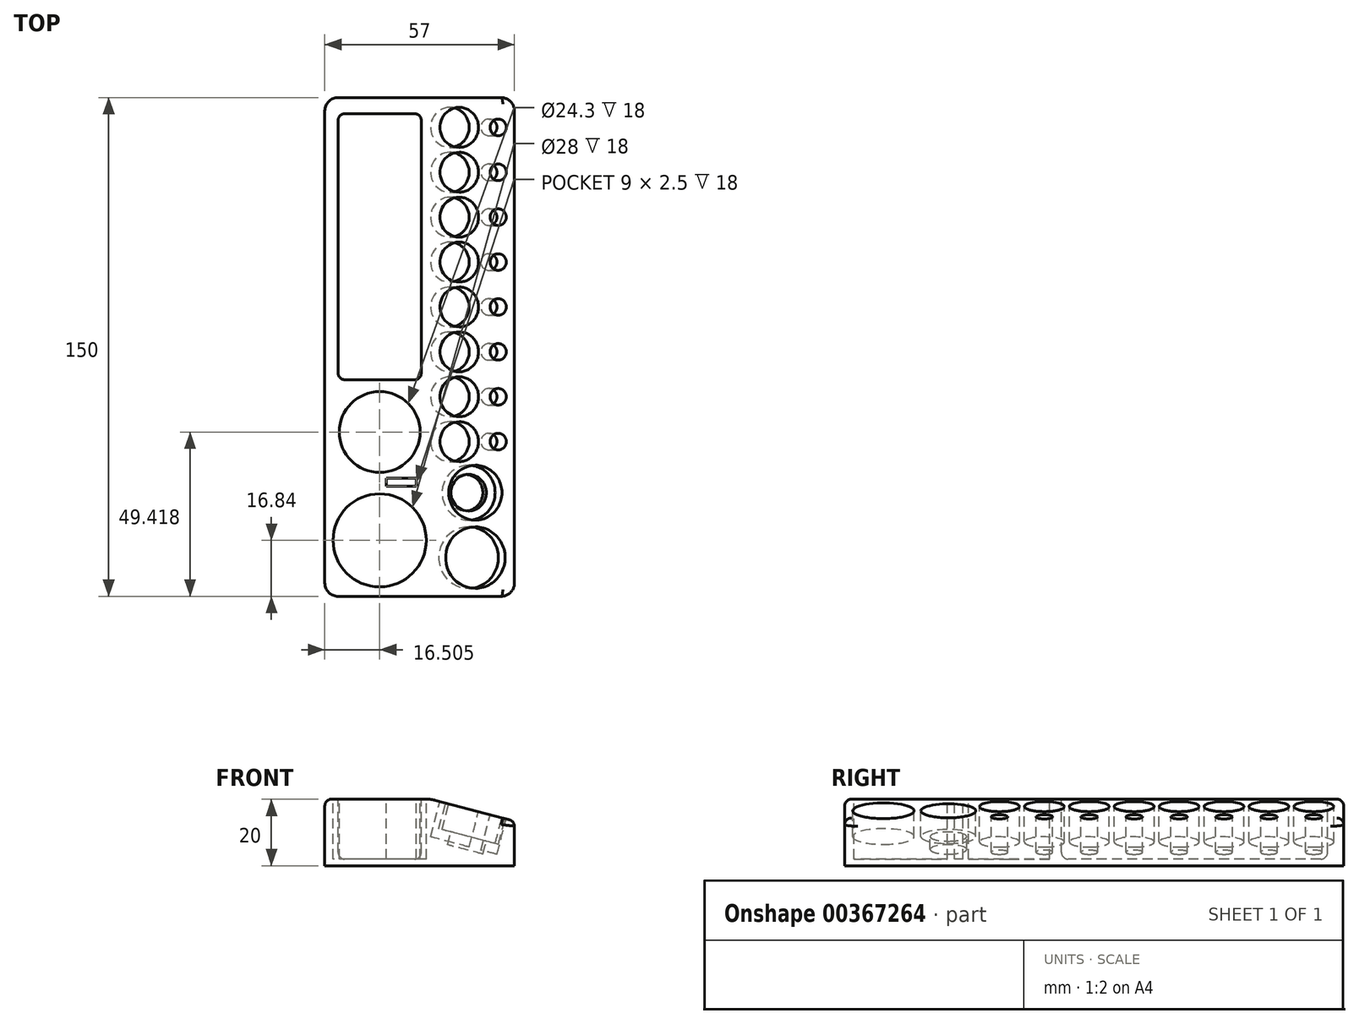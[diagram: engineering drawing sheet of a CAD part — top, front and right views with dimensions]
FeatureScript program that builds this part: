
annotation { "Feature Type Name" : "Feature", "Feature Type Description" : "" }
export const myFeature = defineFeature(function(context is Context, id is Id, definition is map)
    precondition{}
    {
        {
            var Q0;
            Q0=qCreatedBy(makeId("Front.planeOp"),FACE);
            var sketch = newSketch(context, id + "F0", { "sketchPlane" : qUnion([Q0])});
            skLineSegment(sketch, "E0", {"start": v(-10.67, -1.03) * mm, "end": v(-10.67, -21.03) * mm});
            skLineSegment(sketch, "E1", {"start": v(-10.67, -21.03) * mm, "end": v(46.33, -21.03) * mm});
            skLineSegment(sketch, "E2", {"start": v(46.33, -21.03) * mm, "end": v(46.33, -7.6) * mm});
            skLineSegment(sketch, "E3", {"start": v(46.33, -7.6) * mm, "end": v(21.33, -1.03) * mm});
            skLineSegment(sketch, "E4", {"start": v(21.33, -1.03) * mm, "end": v(21.33, -1.03) * mm});
            skLineSegment(sketch, "E5", {"start": v(21.33, -1.03) * mm, "end": v(-10.67, -1.03) * mm});
            skSolve(sketch);
        }
        {
            var Q0;
            Q0=makeQuery(id+"F0.imprint","IMPRINT",FACE,{"disambiguationData":[TD([[makeQuery(id+"F0.imprint","IMPRINT",EDGE,{"derivedFrom":sQuery(id+"F0.wireOp",EDGE,"E0")}),1.0]])]});
            extrude(context, id + "F1", {"entities" : qUnion([Q0]), "endBound" : BoundingType.SYMMETRIC, "depth" : 150 * mm});
        }
        {
            var Q0;
            Q0=makeQuery(id+"F1.opExtrude","SWEPT_FACE",FACE,{"disambiguationData":[OSD([sQuery(id+"F0.wireOp",EDGE,"E3")])]});
            var sketch = newSketch(context, id + "F2", { "sketchPlane" : qUnion([Q0])});
            skCircle(sketch, "E6", {"center": v(34.6, -63.35) * mm, "radius": 9.25 * mm});
            skCircle(sketch, "E7", {"center": v(34.6, -43.82) * mm, "radius": 8.25 * mm});
            skCircle(sketch, "E8", {"center": v(34.6, -43.82) * mm, "radius": 5.5 * mm});
            skCircle(sketch, "E9", {"center": v(29.58, -28.46) * mm, "radius": 6 * mm});
            skCircle(sketch, "E10.0.1.0", {"center": v(29.58, -14.96) * mm, "radius": 6 * mm});
            skCircle(sketch, "E10.0.2.0", {"center": v(29.58, -1.46) * mm, "radius": 6 * mm});
            skCircle(sketch, "E10.0.3.0", {"center": v(29.58, 12.04) * mm, "radius": 6 * mm});
            skCircle(sketch, "E10.0.4.0", {"center": v(29.58, 25.54) * mm, "radius": 6 * mm});
            skCircle(sketch, "E10.0.5.0", {"center": v(29.58, 39.04) * mm, "radius": 6 * mm});
            skCircle(sketch, "E10.0.6.0", {"center": v(29.58, 52.54) * mm, "radius": 6 * mm});
            skLineSegment(sketch, "E10.direction1", {"start": v(29.58, -28.46) * mm, "end": v(53.66, -28.46) * mm, "construction": true});
            skLineSegment(sketch, "E10.direction2", {"start": v(29.58, -28.46) * mm, "end": v(29.58, -14.96) * mm, "construction": true});
            skCircle(sketch, "E11.0.0.7", {"center": v(29.58, 66.04) * mm, "radius": 6 * mm});
            skCircle(sketch, "E12", {"center": v(41.71, -28.46) * mm, "radius": 2.5 * mm});
            skCircle(sketch, "E13.0.1.0", {"center": v(41.71, -14.96) * mm, "radius": 2.5 * mm});
            skCircle(sketch, "E13.0.2.0", {"center": v(41.71, -1.46) * mm, "radius": 2.5 * mm});
            skCircle(sketch, "E13.0.3.0", {"center": v(41.71, 12.04) * mm, "radius": 2.5 * mm});
            skCircle(sketch, "E13.0.4.0", {"center": v(41.71, 25.54) * mm, "radius": 2.5 * mm});
            skCircle(sketch, "E13.0.5.0", {"center": v(41.71, 39.04) * mm, "radius": 2.5 * mm});
            skCircle(sketch, "E13.0.6.0", {"center": v(41.71, 52.54) * mm, "radius": 2.5 * mm});
            skCircle(sketch, "E13.0.7.0", {"center": v(41.71, 66.04) * mm, "radius": 2.5 * mm});
            skLineSegment(sketch, "E13.direction1", {"start": v(41.71, -28.46) * mm, "end": v(64.44, -28.46) * mm, "construction": true});
            skLineSegment(sketch, "E13.direction2", {"start": v(41.71, -28.46) * mm, "end": v(41.71, -14.96) * mm, "construction": true});
            skSolve(sketch);
        }
        {
            var Q0;
            Q0=makeQuery(id+"F2.imprint","IMPRINT",FACE,{"disambiguationData":[TD([[makeQuery(id+"F2.imprint","IMPRINT",EDGE,{"derivedFrom":sQuery(id+"F2.wireOp",EDGE,"E6")}),1.0]])]});
            extrude(context, id + "F3", {"entities" : qUnion([Q0]), "operationType" : NewBodyOperationType.REMOVE, "oppositeDirection" : true, "depth" : 8 * mm});
        }
        {
            var Q0;
            Q0=makeQuery(id+"F2.imprint","IMPRINT",FACE,{"disambiguationData":[TD([[makeQuery(id+"F2.imprint","IMPRINT",EDGE,{"derivedFrom":sQuery(id+"F2.wireOp",EDGE,"E7")}),1.0]])]});
            extrude(context, id + "F4", {"entities" : qUnion([Q0]), "operationType" : NewBodyOperationType.REMOVE, "oppositeDirection" : true, "depth" : 8 * mm});
        }
        {
            var Q0;
            Q0=makeQuery(id+"F4.boolean.opBoolean","SPLIT",FACE,{"disambiguationData":[TD([makeQuery(id+"F4.opExtrude","SWEPT_FACE",FACE,{"disambiguationData":[OSD([sQuery(id+"F2.wireOp",EDGE,"E8")])]})])],"derivedFrom":makeQuery(id+"F1.opExtrude","SWEPT_FACE",FACE,{"disambiguationData":[OSD([sQuery(id+"F0.wireOp",EDGE,"E3")])]})});
            extrude(context, id + "F5", {"entities" : qUnion([Q0]), "operationType" : NewBodyOperationType.REMOVE, "oppositeDirection" : true, "depth" : 12 * mm});
        }
        {
            var Q0;
            Q0=makeQuery(id+"F2.imprint","IMPRINT",FACE,{"disambiguationData":[TD([[makeQuery(id+"F2.imprint","IMPRINT",EDGE,{"derivedFrom":sQuery(id+"F2.wireOp",EDGE,"E13.0.2.0")}),1.0]])]});
            var Q1;
            Q1=makeQuery(id+"F2.imprint","IMPRINT",FACE,{"disambiguationData":[TD([[makeQuery(id+"F2.imprint","IMPRINT",EDGE,{"derivedFrom":sQuery(id+"F2.wireOp",EDGE,"E13.0.3.0")}),1.0]])]});
            var Q2;
            Q2=makeQuery(id+"F2.imprint","IMPRINT",FACE,{"disambiguationData":[TD([[makeQuery(id+"F2.imprint","IMPRINT",EDGE,{"derivedFrom":sQuery(id+"F2.wireOp",EDGE,"E13.0.1.0")}),1.0]])]});
            var Q3;
            Q3=makeQuery(id+"F2.imprint","IMPRINT",FACE,{"disambiguationData":[TD([[makeQuery(id+"F2.imprint","IMPRINT",EDGE,{"derivedFrom":sQuery(id+"F2.wireOp",EDGE,"E12")}),1.0]])]});
            var Q4;
            Q4=makeQuery(id+"F2.imprint","IMPRINT",FACE,{"disambiguationData":[TD([[makeQuery(id+"F2.imprint","IMPRINT",EDGE,{"derivedFrom":sQuery(id+"F2.wireOp",EDGE,"E13.0.4.0")}),1.0]])]});
            var Q5;
            Q5=makeQuery(id+"F2.imprint","IMPRINT",FACE,{"disambiguationData":[TD([[makeQuery(id+"F2.imprint","IMPRINT",EDGE,{"derivedFrom":sQuery(id+"F2.wireOp",EDGE,"E13.0.5.0")}),1.0]])]});
            var Q6;
            Q6=makeQuery(id+"F2.imprint","IMPRINT",FACE,{"disambiguationData":[TD([[makeQuery(id+"F2.imprint","IMPRINT",EDGE,{"derivedFrom":sQuery(id+"F2.wireOp",EDGE,"E13.0.6.0")}),1.0]])]});
            var Q7;
            Q7=makeQuery(id+"F2.imprint","IMPRINT",FACE,{"disambiguationData":[TD([[makeQuery(id+"F2.imprint","IMPRINT",EDGE,{"derivedFrom":sQuery(id+"F2.wireOp",EDGE,"E13.0.7.0")}),1.0]])]});
            extrude(context, id + "F6", {"entities" : qUnion([Q0, Q1, Q2, Q3, Q4, Q5, Q6, Q7]), "operationType" : NewBodyOperationType.REMOVE, "oppositeDirection" : true, "depth" : 11 * mm});
        }
        {
            var Q0;
            Q0=makeQuery(id+"F2.imprint","IMPRINT",FACE,{"disambiguationData":[TD([[makeQuery(id+"F2.imprint","IMPRINT",EDGE,{"derivedFrom":sQuery(id+"F2.wireOp",EDGE,"E9")}),1.0]])]});
            var Q1;
            Q1=makeQuery(id+"F2.imprint","IMPRINT",FACE,{"disambiguationData":[TD([[makeQuery(id+"F2.imprint","IMPRINT",EDGE,{"derivedFrom":sQuery(id+"F2.wireOp",EDGE,"E10.0.1.0")}),1.0]])]});
            var Q2;
            Q2=makeQuery(id+"F2.imprint","IMPRINT",FACE,{"disambiguationData":[TD([[makeQuery(id+"F2.imprint","IMPRINT",EDGE,{"derivedFrom":sQuery(id+"F2.wireOp",EDGE,"E10.0.2.0")}),1.0]])]});
            var Q3;
            Q3=makeQuery(id+"F2.imprint","IMPRINT",FACE,{"disambiguationData":[TD([[makeQuery(id+"F2.imprint","IMPRINT",EDGE,{"derivedFrom":sQuery(id+"F2.wireOp",EDGE,"E10.0.3.0")}),1.0]])]});
            var Q4;
            Q4=makeQuery(id+"F2.imprint","IMPRINT",FACE,{"disambiguationData":[TD([[makeQuery(id+"F2.imprint","IMPRINT",EDGE,{"derivedFrom":sQuery(id+"F2.wireOp",EDGE,"E10.0.4.0")}),1.0]])]});
            var Q5;
            Q5=makeQuery(id+"F2.imprint","IMPRINT",FACE,{"disambiguationData":[TD([[makeQuery(id+"F2.imprint","IMPRINT",EDGE,{"derivedFrom":sQuery(id+"F2.wireOp",EDGE,"E11.0.0.7")}),1.0]])]});
            var Q6;
            Q6=makeQuery(id+"F2.imprint","IMPRINT",FACE,{"disambiguationData":[TD([[makeQuery(id+"F2.imprint","IMPRINT",EDGE,{"derivedFrom":sQuery(id+"F2.wireOp",EDGE,"E10.0.6.0")}),1.0]])]});
            var Q7;
            Q7=makeQuery(id+"F2.imprint","IMPRINT",FACE,{"disambiguationData":[TD([[makeQuery(id+"F2.imprint","IMPRINT",EDGE,{"derivedFrom":sQuery(id+"F2.wireOp",EDGE,"E10.0.5.0")}),1.0]])]});
            extrude(context, id + "F7", {"entities" : qUnion([Q0, Q1, Q2, Q3, Q4, Q5, Q6, Q7]), "operationType" : NewBodyOperationType.REMOVE, "oppositeDirection" : true, "depth" : 11 * mm});
        }
        {
            var Q0;
            Q0=makeQuery(id+"F1.opExtrude","SWEPT_FACE",FACE,{"disambiguationData":[OSD([sQuery(id+"F0.wireOp",EDGE,"E5")])]});
            var sketch = newSketch(context, id + "F8", { "sketchPlane" : qUnion([Q0])});
            skCircle(sketch, "E14", {"center": v(5.83, -58.16) * mm, "radius": 14 * mm});
            skCircle(sketch, "E15", {"center": v(5.83, -25.58) * mm, "radius": 12.15 * mm});
            skLineSegment(sketch, "E16.bottom", {"start": v(16.88, -39.43) * mm, "end": v(7.88, -39.43) * mm});
            skLineSegment(sketch, "E16.top", {"start": v(16.88, -41.93) * mm, "end": v(7.88, -41.93) * mm});
            skLineSegment(sketch, "E16.left", {"start": v(16.88, -39.43) * mm, "end": v(16.88, -41.93) * mm});
            skLineSegment(sketch, "E16.right", {"start": v(7.88, -39.43) * mm, "end": v(7.88, -41.93) * mm});
            skPoint(sketch, "E16.middle", {"position": v(12.38, -40.68) * mm});
            skLineSegment(sketch, "E17.bottom", {"start": v(18.33, 70.15) * mm, "end": v(-6.67, 70.15) * mm});
            skLineSegment(sketch, "E17.top", {"start": v(18.33, -9.85) * mm, "end": v(-6.67, -9.85) * mm});
            skLineSegment(sketch, "E17.left", {"start": v(18.33, 70.15) * mm, "end": v(18.33, -9.85) * mm});
            skLineSegment(sketch, "E17.right", {"start": v(-6.67, 70.15) * mm, "end": v(-6.67, -9.85) * mm});
            skPoint(sketch, "E17.middle", {"position": v(5.83, 30.15) * mm});
            skSolve(sketch);
        }
        {
            var Q0;
            Q0=makeQuery(id+"F8.imprint","IMPRINT",FACE,{"disambiguationData":[TD([[makeQuery(id+"F8.imprint","IMPRINT",EDGE,{"derivedFrom":sQuery(id+"F8.wireOp",EDGE,"E15")}),1.0]])]});
            var Q1;
            Q1=makeQuery(id+"F8.imprint","IMPRINT",FACE,{"disambiguationData":[TD([[makeQuery(id+"F8.imprint","IMPRINT",EDGE,{"derivedFrom":sQuery(id+"F8.wireOp",EDGE,"E14")}),1.0]])]});
            var Q2;
            Q2=makeQuery(id+"F8.imprint","IMPRINT",FACE,{"disambiguationData":[TD([[makeQuery(id+"F8.imprint","IMPRINT",EDGE,{"derivedFrom":sQuery(id+"F8.wireOp",EDGE,"E16.bottom")}),1.0]])]});
            var Q3;
            Q3=makeQuery(id+"F8.imprint","IMPRINT",FACE,{"disambiguationData":[TD([[makeQuery(id+"F8.imprint","IMPRINT",EDGE,{"derivedFrom":sQuery(id+"F8.wireOp",EDGE,"E17.bottom")}),1.0]])]});
            extrude(context, id + "F9", {"entities" : qUnion([Q0, Q1, Q2, Q3]), "operationType" : NewBodyOperationType.REMOVE, "oppositeDirection" : true, "depth" : 18 * mm});
        }
        {
            var Q0;
            Q0=makeQuery(id+"F9.boolean.opBoolean","COPY",FACE,{"derivedFrom":makeQuery(id+"F9.opExtrude","CAP_FACE",FACE,{"disambiguationData":[OSD([sQuery(id+"F8.wireOp",EDGE,"E17.bottom"),sQuery(id+"F8.wireOp",EDGE,"E17.top"),sQuery(id+"F8.wireOp",EDGE,"E17.left"),sQuery(id+"F8.wireOp",EDGE,"E17.right")])],"isStart":false})});
            var Q1;
            Q1=makeQuery(id+"F9.boolean.opBoolean","COPY",EDGE,{"derivedFrom":makeQuery(id+"F9.opExtrude","CAP_EDGE",EDGE,{"disambiguationData":[OSD([sQuery(id+"F8.wireOp",EDGE,"E17.right")])],"isStart":true})});
            var Q2;
            Q2=makeQuery(id+"F9.boolean.opBoolean","COPY",EDGE,{"derivedFrom":makeQuery(id+"F9.opExtrude","CAP_EDGE",EDGE,{"disambiguationData":[OSD([sQuery(id+"F8.wireOp",EDGE,"E17.top")])],"isStart":true})});
            var Q3;
            Q3=makeQuery(id+"F9.boolean.opBoolean","COPY",EDGE,{"derivedFrom":makeQuery(id+"F9.opExtrude","CAP_EDGE",EDGE,{"disambiguationData":[OSD([sQuery(id+"F8.wireOp",EDGE,"E17.left")])],"isStart":true})});
            var Q4;
            Q4=makeQuery(id+"F9.boolean.opBoolean","COPY",EDGE,{"derivedFrom":makeQuery(id+"F9.opExtrude","CAP_EDGE",EDGE,{"disambiguationData":[OSD([sQuery(id+"F8.wireOp",EDGE,"E17.bottom")])],"isStart":true})});
            var Q5;
            Q5=makeQuery(id+"F9.boolean.opBoolean","COPY",EDGE,{"derivedFrom":makeQuery(id+"F9.opExtrude","SWEPT_EDGE",EDGE,{"disambiguationData":[OSD([sQuery(id+"F8.wireOp",EDGE,"E17.top"),sQuery(id+"F8.wireOp",EDGE,"E17.right")])]})});
            var Q6;
            Q6=makeQuery(id+"F9.boolean.opBoolean","COPY",EDGE,{"derivedFrom":makeQuery(id+"F9.opExtrude","SWEPT_EDGE",EDGE,{"disambiguationData":[OSD([sQuery(id+"F8.wireOp",EDGE,"E17.top"),sQuery(id+"F8.wireOp",EDGE,"E17.left")])]})});
            var Q7;
            Q7=makeQuery(id+"F9.boolean.opBoolean","COPY",EDGE,{"derivedFrom":makeQuery(id+"F9.opExtrude","SWEPT_EDGE",EDGE,{"disambiguationData":[OSD([sQuery(id+"F8.wireOp",EDGE,"E17.bottom"),sQuery(id+"F8.wireOp",EDGE,"E17.right")])]})});
            var Q8;
            Q8=makeQuery(id+"F9.boolean.opBoolean","COPY",EDGE,{"derivedFrom":makeQuery(id+"F9.opExtrude","SWEPT_EDGE",EDGE,{"disambiguationData":[OSD([sQuery(id+"F8.wireOp",EDGE,"E17.bottom"),sQuery(id+"F8.wireOp",EDGE,"E17.left")])]})});
            var Q9;
            Q9=makeQuery(id+"F1.opExtrude","SWEPT_EDGE",EDGE,{"disambiguationData":[OSD([sQuery(id+"F0.wireOp",EDGE,"E0"),sQuery(id+"F0.wireOp",EDGE,"E5")])]});
            var Q10;
            Q10=makeQuery(id+"F1.opExtrude","CAP_EDGE",EDGE,{"disambiguationData":[OSD([sQuery(id+"F0.wireOp",EDGE,"E5")])],"isStart":false});
            var Q11;
            Q11=makeQuery(id+"F1.opExtrude","CAP_EDGE",EDGE,{"disambiguationData":[OSD([sQuery(id+"F0.wireOp",EDGE,"E3")])],"isStart":false});
            var Q12;
            Q12=makeQuery(id+"F1.opExtrude","CAP_EDGE",EDGE,{"disambiguationData":[OSD([sQuery(id+"F0.wireOp",EDGE,"E3")])],"isStart":true});
            var Q13;
            Q13=makeQuery(id+"F1.opExtrude","CAP_EDGE",EDGE,{"disambiguationData":[OSD([sQuery(id+"F0.wireOp",EDGE,"E5")])],"isStart":true});
            var Q14;
            Q14=makeQuery(id+"F1.opExtrude","SWEPT_EDGE",EDGE,{"disambiguationData":[OSD([sQuery(id+"F0.wireOp",EDGE,"E2"),sQuery(id+"F0.wireOp",EDGE,"E3")])]});
            fillet(context, id + "F10", {"entities" : qUnion([Q0, Q1, Q2, Q3, Q4, Q5, Q6, Q7, Q8, Q9, Q10, Q11, Q12, Q13, Q14]), "radius" : 2 * mm, "tangentPropagation" : true, "allowEdgeOverflow" : false});
        }
        {
            var Q0;
            Q0=makeQuery(id+"F1.opExtrude","SWEPT_EDGE",EDGE,{"disambiguationData":[OSD([sQuery(id+"F0.wireOp",EDGE,"E3"),sQuery(id+"F0.wireOp",EDGE,"E5")])]});
            fillet(context, id + "F11", {"entities" : qUnion([Q0]), "radius" : 10 * mm, "tangentPropagation" : true, "allowEdgeOverflow" : false});
        }
        {
            var Q0;
            Q0=makeQuery(id+"F1.opExtrude","CAP_EDGE",EDGE,{"disambiguationData":[OSD([sQuery(id+"F0.wireOp",EDGE,"E0")])],"isStart":true});
            var Q1;
            Q1=makeQuery(id+"F1.opExtrude","CAP_EDGE",EDGE,{"disambiguationData":[OSD([sQuery(id+"F0.wireOp",EDGE,"E2")])],"isStart":true});
            var Q2;
            Q2=makeQuery(id+"F1.opExtrude","CAP_EDGE",EDGE,{"disambiguationData":[OSD([sQuery(id+"F0.wireOp",EDGE,"E2")])],"isStart":false});
            var Q3;
            Q3=makeQuery(id+"F1.opExtrude","CAP_EDGE",EDGE,{"disambiguationData":[OSD([sQuery(id+"F0.wireOp",EDGE,"E0")])],"isStart":false});
            fillet(context, id + "F12", {"entities" : qUnion([Q0, Q1, Q2, Q3]), "radius" : 4 * mm, "tangentPropagation" : true, "allowEdgeOverflow" : false});
        }
    });
